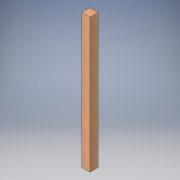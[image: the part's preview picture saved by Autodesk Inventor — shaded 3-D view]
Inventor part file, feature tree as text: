
AUTODESK INVENTOR PART (.ipt)
format: ipt  version: 2016 (Build 200138000, 138)  size: 95,744 bytes
history: native  units: in
note: dims shown in document units (in); Inventor stores cm internally (conversion verified against a paired STEP export)
features: extrude x1, sketch x1
ambient origin geometry x8: Origin, YZ Plane, XZ Plane, XY Plane, X Axis, Y Axis, Z Axis, Center Point
bodies: Solid1 (feature_tree)
feature tree (2):
  extrude  "Extrusion1"  Depth=57.0in TaperAngle=0.0deg
  sketch  "Sketch1"  dims[d0=3.5in d1=57.0in d2=0.0in]
